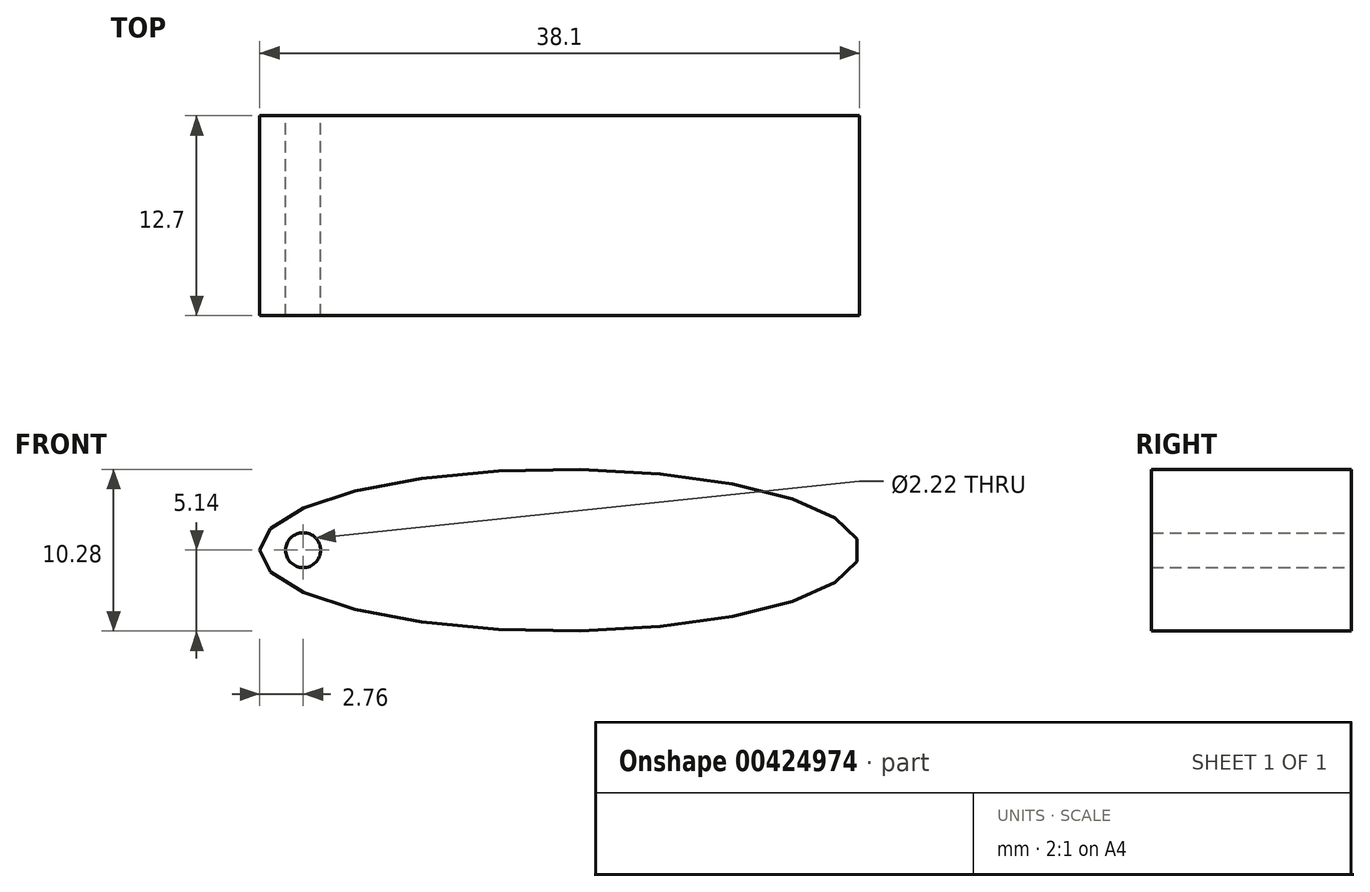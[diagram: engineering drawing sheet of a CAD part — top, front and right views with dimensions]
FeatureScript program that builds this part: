
annotation { "Feature Type Name" : "Feature", "Feature Type Description" : "" }
export const myFeature = defineFeature(function(context is Context, id is Id, definition is map)
    precondition{}
    {
        {
            var Q0;
            Q0=qCreatedBy(makeId("Front.planeOp"),FACE);
            var sketch = newSketch(context, id + "F0", { "sketchPlane" : qUnion([Q0])});
            skEllipse(sketch, "E0", {"center": v(0, 0) * mm, "majorRadius": 19.05 * mm, "minorRadius": 5.14 * mm, "majorAxis": v(-1, 0)});
            skCircle(sketch, "E1", {"center": v(-16.29, 0) * mm, "radius": 1.1 * mm});
            skSolve(sketch);
        }
        {
            var Q0;
            Q0=makeQuery(id+"F0.imprint","IMPRINT",FACE,{"disambiguationData":[TD([[makeQuery(id+"F0.imprint","IMPRINT",EDGE,{"derivedFrom":sQuery(id+"F0.wireOp",EDGE,"E0")}),1.0]])]});
            extrude(context, id + "F1", {"entities" : qUnion([Q0]), "depth" : 12.7 * mm});
        }
    });
